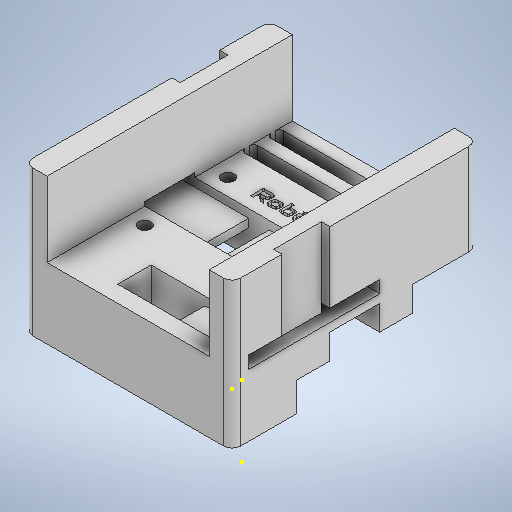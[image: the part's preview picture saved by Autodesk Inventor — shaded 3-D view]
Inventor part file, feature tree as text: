
AUTODESK INVENTOR PART (.ipt)
format: ipt  version: 2025.2 (Build 292293000, 293)  size: 969,216 bytes
history: native  units: mm
features: sketch x38, extrude x35, thread x7, other x1
ambient origin geometry x8: Origin, YZ Plane, XZ Plane, XY Plane, X Axis, Y Axis, Z Axis, Center Point
bodies: Body1 (feature_tree)
feature tree (81):
  other  "Sólido1"
  extrude  "Extrusão1"  Depth=59.0mm
  extrude  "Extrusão2"  Depth=5.0mm TaperAngle=0.0deg
  extrude  "Extrusão3"  Depth=15.5mm
  extrude  "Extrusão4"  Depth=8.0mm
  thread  "Rosca1"  [1 undecoded]
  thread  "Rosca2"  [1 undecoded]
  thread  "Rosca3"  [1 undecoded]
  thread  "Rosca4"  [1 undecoded]
  thread  "Rosca5"  [1 undecoded]
  thread  "Rosca6"  [1 undecoded]
  thread  "Rosca7"  [1 undecoded]
  extrude  "Extrusão7"  Depth=4.0mm
  sketch  "Esboço9"  dims[d20=3.0mm d21=3.0mm]
  extrude  "Extrusão9"  Depth=3.0mm
  extrude  "Extrusão10"  Depth=3.0mm
  extrude  "Extrusão11"  Depth=11.0mm TaperAngle=0.0deg
  extrude  "Extrusão12"  Depth=9.0mm TaperAngle=0.0deg
  extrude  "Extrusão13"  Depth=11.0mm TaperAngle=0.0deg
  extrude  "Extrusão14"  Depth=11.0mm TaperAngle=0.0deg
  extrude  "Extrusão15"  Depth=6.0mm TaperAngle=0.0deg
  extrude  "Extrusão18"  Depth=13.0mm TaperAngle=0.0deg
  extrude  "Extrusão20"  Depth=16.0mm TaperAngle=0.0deg
  sketch  "Esboço24"  dims[d70=2.0mm d71=0.0mm d72=17.0mm d73=0.0mm]
  extrude  "Extrusão22"  Depth=17.0mm TaperAngle=0.0deg
  extrude  "Extrusão23"  TaperAngle=0.0deg  [1 undecoded]
  extrude  "Extrusão24"  Depth=2.0mm TaperAngle=0.0deg
  sketch  "Esboço26"  dims[d114=2.0mm d115=0.0mm d118=36.0mm d119=0.0mm]
  extrude  "Extrusão25"  Depth=5.5mm
  extrude  "Extrusão26"  Depth=5.5mm
  extrude  "Extrusão27"  Depth=2.0mm TaperAngle=0.0deg
  sketch  "Esboço30"  dims[d132=2.0mm d133=0.0mm d134=0.0mm]
  sketch  "Esboço31"  dims[d135=1.0mm d136=0.0mm d137=1.0mm d138=0.0mm]
  extrude  "Extrusão28"  TaperAngle=0.0deg  [1 undecoded]
  sketch  "Esboço32"  dims[d139=1.0mm d140=0.0mm d141=2.0mm d142=0.0mm]
  extrude  "Extrusão29"  Depth=1.0mm TaperAngle=0.0deg
  extrude  "Extrusão30"  Depth=2.0mm TaperAngle=0.0deg
  extrude  "Extrusão31"  Depth=17.0mm TaperAngle=0.0deg
  extrude  "Extrusão32"  Depth=2.0mm TaperAngle=0.0deg
  extrude  "Extrusão33"  Depth=4.0mm TaperAngle=0.0deg
  extrude  "Extrusão34"  Depth=2.0mm
  extrude  "Extrusão35"  Depth=5.0mm
  extrude  "Extrusão36"  Depth=2.0mm
  extrude  "Extrusão37"  Depth=2.0mm TaperAngle=0.0deg
  extrude  "Extrusão38"  Depth=1.0mm TaperAngle=0.0deg
  sketch  "Esboço42"  dims[d171=1.9mm d172=1.9mm]
  sketch  "Esboço43"  dims[d173=14.0mm d174=0.0mm d175=14.0mm d176=0.0mm]
  extrude  "Extrusão39"  Depth=1.9mm
  extrude  "Extrusão40"  Depth=1.9mm
  extrude  "Extrusão41"  Depth=14.0mm TaperAngle=0.0deg
  extrude  "Extrusão42"  Depth=0.872665mm
  sketch  "Esboço1"  dims[d0=55.0mm d1=59.0mm]
  sketch  "Esboço2"  dims[d2=5.0mm d3=5.0mm d4=0.0mm]
  sketch  "Esboço3"  dims[d5=15.5mm d6=15.5mm]
  sketch  "Esboço4"  dims[d7=8.0mm d8=8.0mm d9=6.0mm d10=0.0mm d11=16.0mm d12=0.0mm d13=4.0mm d14=12.0mm d15=4.0mm d16=12.0mm d17=4.0mm]
  sketch  "Esboço7"  dims[d18=12.0mm d19=4.0mm]
  sketch  "Esboço10"  dims[d22=3.0mm d23=3.0mm]
  sketch  "Esboço11"  dims[d24=11.0mm d25=0.0mm d26=11.0mm d27=0.0mm]
  sketch  "Esboço12"  dims[d28=9.0mm d29=0.0mm d30=9.0mm d31=0.0mm]
  sketch  "Esboço13"  dims[d32=9.0mm d33=0.0mm d41=11.0mm d42=0.0mm]
  sketch  "Esboço14"  dims[d43=11.0mm d44=0.0mm d45=11.0mm d46=0.0mm]
  sketch  "Esboço16"  dims[d47=6.0mm d48=0.0mm d53=19.0mm d54=0.0mm]
  sketch  "Esboço20"  dims[d55=2.0mm d56=0.0mm d57=13.0mm d58=0.0mm]
  sketch  "Esboço22"  dims[d66=1.0mm d67=0.0mm d68=16.0mm d69=0.0mm]
  sketch  "Esboço25"  dims[d97=1.0mm d98=0.0mm d99=0.0mm]
  sketch  "Esboço27"  dims[d120=23.0mm d121=0.0mm d125=5.5mm]
  sketch  "Esboço28"  dims[d126=5.5mm d127=59.0mm]
  sketch  "Esboço29"  dims[d128=0.0mm d129=0.0mm d130=2.0mm d131=0.0mm]
  sketch  "Esboço33"  dims[d143=11.5mm d144=17.0mm d145=0.0mm]
  sketch  "Esboço34"  dims[d146=1.0mm d147=0.0mm d148=2.0mm d149=0.0mm]
  sketch  "Esboço35"  dims[d150=2.0mm d151=0.0mm d152=4.0mm d153=0.0mm]
  sketch  "Esboço36"  dims[d154=2.0mm d155=0.0mm d156=2.5mm]
  sketch  "Esboço37"  dims[d157=8.0mm d158=5.0mm]
  sketch  "Esboço38"  dims[d159=2.0mm d160=0.0mm d161=2.5mm]
  sketch  "Esboço39"  dims[d162=5.0mm d163=2.0mm d164=0.0mm]
  sketch  "Esboço40"  dims[d165=1.0mm d166=0.0mm d167=1.0mm d168=0.0mm]
  sketch  "Esboço41"  dims[d169=1.9mm d170=1.9mm]
  sketch  "Esboço44"  dims[d90=0.5mm d91=0.872665mm]
  sketch  "Esboço45"  dims[d92=0.5mm]
  sketch  "Esboço46"  dims[d93=0.872665mm]
  sketch  "Esboço47"
note: 9 required parameter values undecoded (feature->parameter linkage not recoverable at this tier; creation-order binding heuristic only, values carry confidence <= 0.55)
